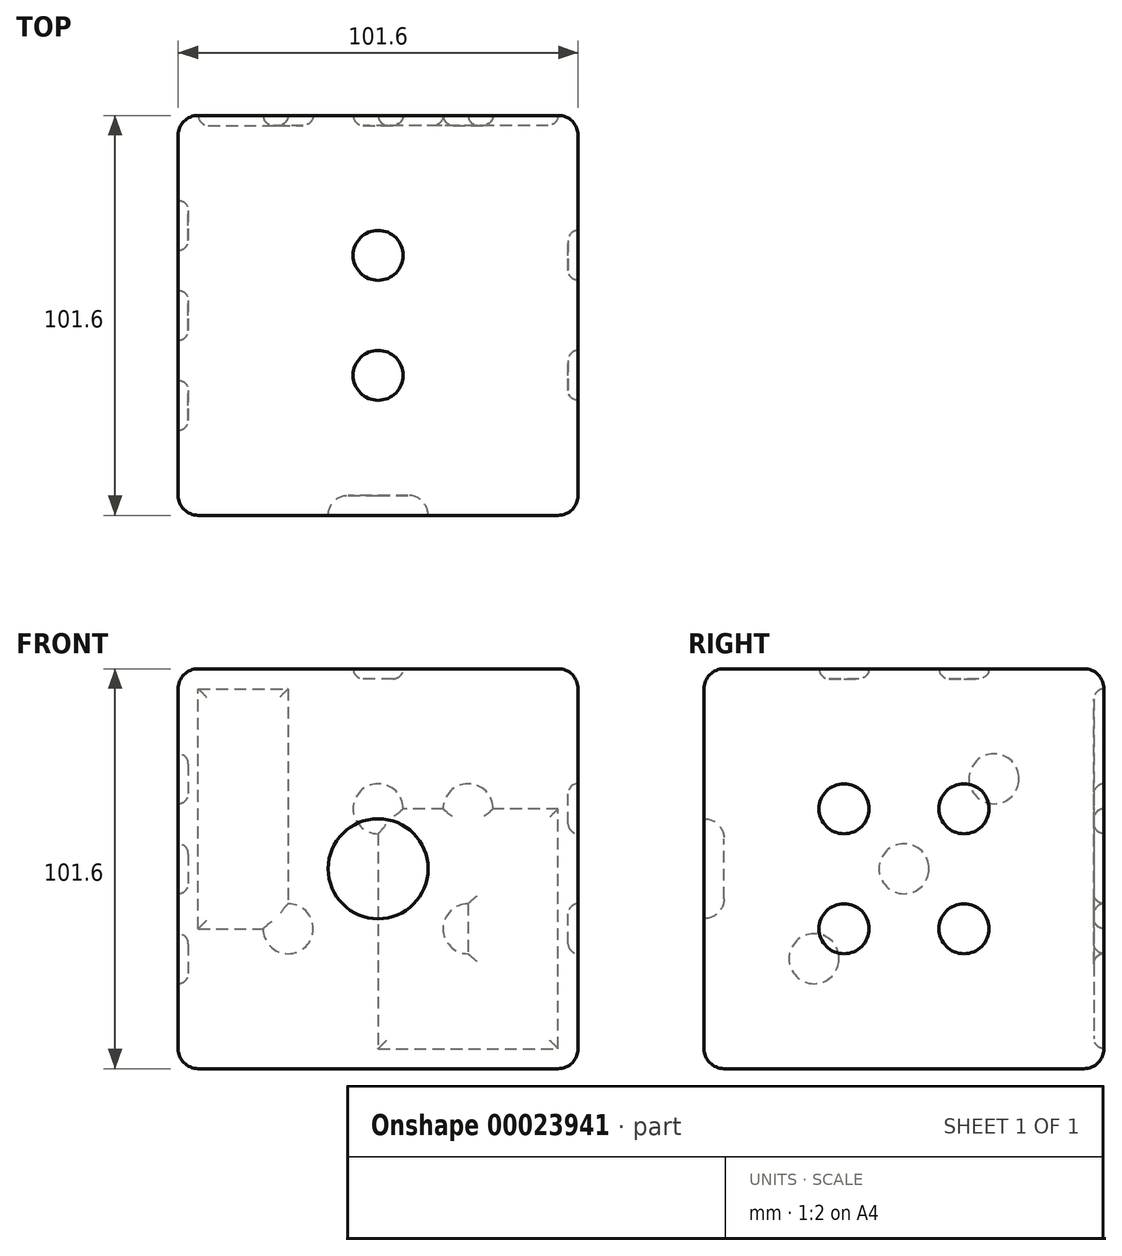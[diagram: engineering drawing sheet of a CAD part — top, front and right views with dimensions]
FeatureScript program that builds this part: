
annotation { "Feature Type Name" : "Feature", "Feature Type Description" : "" }
export const myFeature = defineFeature(function(context is Context, id is Id, definition is map)
    precondition{}
    {
        {
            var Q0;
            Q0=qCreatedBy(makeId("Front.planeOp"),FACE);
            var sketch = newSketch(context, id + "F0", { "sketchPlane" : qUnion([Q0])});
            skLineSegment(sketch, "E0.bottom", {"start": v(0, 0) * mm, "end": v(101.6, 0) * mm});
            skLineSegment(sketch, "E0.top", {"start": v(0, 101.6) * mm, "end": v(101.6, 101.6) * mm});
            skLineSegment(sketch, "E0.left", {"start": v(0, 0) * mm, "end": v(0, 101.6) * mm});
            skLineSegment(sketch, "E0.right", {"start": v(101.6, 0) * mm, "end": v(101.6, 101.6) * mm});
            skSolve(sketch);
        }
        {
            var Q0;
            Q0 = qSketchRegion(id + "F0", true);
            extrude(context, id + "F1", {"entities" : qUnion([Q0]), "depth" : 101.6 * mm});
        }
        {
            var Q0;
            Q0=makeQuery(id+"F1.opExtrude","CAP_FACE",FACE,{"disambiguationData":[OSD([sQuery(id+"F0.wireOp",EDGE,"E0.bottom"),sQuery(id+"F0.wireOp",EDGE,"E0.top"),sQuery(id+"F0.wireOp",EDGE,"E0.left"),sQuery(id+"F0.wireOp",EDGE,"E0.right")])],"isStart":true});
            var Q1;
            Q1=makeQuery(id+"F1.opExtrude","CAP_FACE",FACE,{"disambiguationData":[OSD([sQuery(id+"F0.wireOp",EDGE,"E0.bottom"),sQuery(id+"F0.wireOp",EDGE,"E0.top"),sQuery(id+"F0.wireOp",EDGE,"E0.left"),sQuery(id+"F0.wireOp",EDGE,"E0.right")])],"isStart":false});
            var Q2;
            Q2=makeQuery(id+"F1.opExtrude","SWEPT_FACE",FACE,{"disambiguationData":[OSD([sQuery(id+"F0.wireOp",EDGE,"E0.top")])]});
            var Q3;
            Q3=makeQuery(id+"F1.opExtrude","SWEPT_FACE",FACE,{"disambiguationData":[OSD([sQuery(id+"F0.wireOp",EDGE,"E0.bottom")])]});
            fillet(context, id + "F2", {"entities" : qUnion([Q0, Q1, Q2, Q3]), "radius" : 5.08 * mm, "tangentPropagation" : true, "allowEdgeOverflow" : false});
        }
        {
            var Q0;
            Q0=makeQuery(id+"F1.opExtrude","CAP_FACE",FACE,{"disambiguationData":[OSD([sQuery(id+"F0.wireOp",EDGE,"E0.bottom"),sQuery(id+"F0.wireOp",EDGE,"E0.top"),sQuery(id+"F0.wireOp",EDGE,"E0.left"),sQuery(id+"F0.wireOp",EDGE,"E0.right")])],"isStart":false});
            var sketch = newSketch(context, id + "F3", { "sketchPlane" : qUnion([Q0])});
            skCircle(sketch, "E1", {"center": v(50.8, 50.8) * mm, "radius": 12.7 * mm});
            skSolve(sketch);
        }
        {
            var Q0;
            Q0=makeQuery(id+"F3.imprint","IMPRINT",FACE,{"disambiguationData":[TD([[makeQuery(id+"F3.imprint","IMPRINT",EDGE,{"derivedFrom":sQuery(id+"F3.wireOp",EDGE,"E1")}),1.0]])]});
            extrude(context, id + "F4", {"entities" : qUnion([Q0]), "operationType" : NewBodyOperationType.REMOVE, "oppositeDirection" : true, "depth" : 5.08 * mm});
        }
        {
            var Q0;
            Q0=makeQuery(id+"F4.boolean.opBoolean","COPY",FACE,{"derivedFrom":makeQuery(id+"F4.opExtrude","CAP_FACE",FACE,{"disambiguationData":[OSD([sQuery(id+"F3.wireOp",EDGE,"E1")])],"isStart":false})});
            fillet(context, id + "F5", {"entities" : qUnion([Q0]), "radius" : 5.08 * mm, "tangentPropagation" : true, "allowEdgeOverflow" : false});
        }
        {
            var Q0;
            Q0=makeQuery(id+"F1.opExtrude","CAP_FACE",FACE,{"disambiguationData":[OSD([sQuery(id+"F0.wireOp",EDGE,"E0.bottom"),sQuery(id+"F0.wireOp",EDGE,"E0.top"),sQuery(id+"F0.wireOp",EDGE,"E0.left"),sQuery(id+"F0.wireOp",EDGE,"E0.right")])],"isStart":true});
            var sketch = newSketch(context, id + "F6", { "sketchPlane" : qUnion([Q0])});
            skLineSegment(sketch, "E2", {"start": v(-96.52, 66.04) * mm, "end": v(-5.08, 66.04) * mm});
            skLineSegment(sketch, "E3", {"start": v(-5.08, 35.56) * mm, "end": v(-96.52, 35.56) * mm});
            skLineSegment(sketch, "E4", {"start": v(-73.66, 96.52) * mm, "end": v(-73.66, 5.08) * mm});
            skLineSegment(sketch, "E5", {"start": v(-50.8, 96.52) * mm, "end": v(-50.8, 5.08) * mm});
            skLineSegment(sketch, "E6", {"start": v(-27.94, 96.52) * mm, "end": v(-27.94, 5.08) * mm});
            skCircle(sketch, "E7", {"center": v(-73.66, 66.04) * mm, "radius": 6.35 * mm});
            skCircle(sketch, "E8", {"center": v(-50.8, 66.04) * mm, "radius": 6.35 * mm});
            skCircle(sketch, "E9", {"center": v(-27.94, 66.04) * mm, "radius": 6.35 * mm});
            skCircle(sketch, "E10", {"center": v(-27.94, 35.56) * mm, "radius": 6.35 * mm});
            skCircle(sketch, "E11", {"center": v(-50.8, 35.56) * mm, "radius": 6.35 * mm});
            skCircle(sketch, "E12", {"center": v(-73.66, 35.56) * mm, "radius": 6.35 * mm});
            skSolve(sketch);
        }
        {
            var Q0;
            {var subQ1=sQuery(id+"F6.wireOp",EDGE,"E4");var subQ3=sQuery(id+"F6.wireOp",EDGE,"E2");var subQ5=makeQuery(id+"F6.imprint","INTERSECT",VERTEX,{"derivedFrom":[subQ3,subQ1]});Q0=makeQuery(id+"F6.imprint","IMPRINT",FACE,{"disambiguationData":[TD([[makeQuery(id+"F6.imprint","IMPRINT",EDGE,{"disambiguationData":[TD([[subQ5,-1.0]])],"derivedFrom":subQ3}),1.0]])]});}
            var Q1;
            {var subQ1=sQuery(id+"F6.wireOp",EDGE,"E4");var subQ3=sQuery(id+"F6.wireOp",EDGE,"E2");var subQ5=makeQuery(id+"F6.imprint","INTERSECT",VERTEX,{"derivedFrom":[subQ3,subQ1]});Q1=makeQuery(id+"F6.imprint","IMPRINT",FACE,{"disambiguationData":[TD([[makeQuery(id+"F6.imprint","IMPRINT",EDGE,{"disambiguationData":[TD([[subQ5,-1.0]])],"derivedFrom":subQ3}),-1.0]])]});}
            var Q2;
            {var subQ0=sQuery(id+"F6.wireOp",EDGE,"E7");var subQ3=sQuery(id+"F6.wireOp",EDGE,"E2");var subQ4=makeQuery(id+"F6.imprint","INTERSECT",VERTEX,{"disambiguationData":[OD(0.0)],"derivedFrom":[subQ3,subQ0]});Q2=makeQuery(id+"F6.imprint","IMPRINT",FACE,{"disambiguationData":[TD([[makeQuery(id+"F6.imprint","IMPRINT",EDGE,{"disambiguationData":[TD([[subQ4,-1.0]])],"derivedFrom":subQ3}),-1.0]])]});}
            var Q3;
            {var subQ0=sQuery(id+"F6.wireOp",EDGE,"E7");var subQ3=sQuery(id+"F6.wireOp",EDGE,"E2");var subQ4=makeQuery(id+"F6.imprint","INTERSECT",VERTEX,{"disambiguationData":[OD(0.0)],"derivedFrom":[subQ3,subQ0]});Q3=makeQuery(id+"F6.imprint","IMPRINT",FACE,{"disambiguationData":[TD([[makeQuery(id+"F6.imprint","IMPRINT",EDGE,{"disambiguationData":[TD([[subQ4,-1.0]])],"derivedFrom":subQ3}),1.0]])]});}
            var Q4;
            {var subQ0=sQuery(id+"F6.wireOp",EDGE,"E8");var subQ3=sQuery(id+"F6.wireOp",EDGE,"E2");var subQ4=makeQuery(id+"F6.imprint","INTERSECT",VERTEX,{"disambiguationData":[OD(0.0)],"derivedFrom":[subQ3,subQ0]});Q4=makeQuery(id+"F6.imprint","IMPRINT",FACE,{"disambiguationData":[TD([[makeQuery(id+"F6.imprint","IMPRINT",EDGE,{"disambiguationData":[TD([[subQ4,-1.0]])],"derivedFrom":subQ3}),1.0]])]});}
            var Q5;
            {var subQ1=sQuery(id+"F6.wireOp",EDGE,"E5");var subQ3=sQuery(id+"F6.wireOp",EDGE,"E2");var subQ5=makeQuery(id+"F6.imprint","INTERSECT",VERTEX,{"derivedFrom":[subQ3,subQ1]});Q5=makeQuery(id+"F6.imprint","IMPRINT",FACE,{"disambiguationData":[TD([[makeQuery(id+"F6.imprint","IMPRINT",EDGE,{"disambiguationData":[TD([[subQ5,-1.0]])],"derivedFrom":subQ3}),1.0]])]});}
            var Q6;
            {var subQ1=sQuery(id+"F6.wireOp",EDGE,"E5");var subQ3=sQuery(id+"F6.wireOp",EDGE,"E2");var subQ5=makeQuery(id+"F6.imprint","INTERSECT",VERTEX,{"derivedFrom":[subQ3,subQ1]});Q6=makeQuery(id+"F6.imprint","IMPRINT",FACE,{"disambiguationData":[TD([[makeQuery(id+"F6.imprint","IMPRINT",EDGE,{"disambiguationData":[TD([[subQ5,-1.0]])],"derivedFrom":subQ3}),-1.0]])]});}
            var Q7;
            {var subQ1=sQuery(id+"F6.wireOp",EDGE,"E8");var subQ3=sQuery(id+"F6.wireOp",EDGE,"E2");var subQ5=makeQuery(id+"F6.imprint","INTERSECT",VERTEX,{"disambiguationData":[OD(0.0)],"derivedFrom":[subQ3,subQ1]});Q7=makeQuery(id+"F6.imprint","IMPRINT",FACE,{"disambiguationData":[TD([[makeQuery(id+"F6.imprint","IMPRINT",EDGE,{"disambiguationData":[TD([[subQ5,-1.0]])],"derivedFrom":subQ3}),-1.0]])]});}
            var Q8;
            {var subQ1=sQuery(id+"F6.wireOp",EDGE,"E6");var subQ3=sQuery(id+"F6.wireOp",EDGE,"E2");var subQ5=makeQuery(id+"F6.imprint","INTERSECT",VERTEX,{"derivedFrom":[subQ3,subQ1]});Q8=makeQuery(id+"F6.imprint","IMPRINT",FACE,{"disambiguationData":[TD([[makeQuery(id+"F6.imprint","IMPRINT",EDGE,{"disambiguationData":[TD([[subQ5,-1.0]])],"derivedFrom":subQ3}),1.0]])]});}
            var Q9;
            {var subQ0=sQuery(id+"F6.wireOp",EDGE,"E9");var subQ3=sQuery(id+"F6.wireOp",EDGE,"E2");var subQ4=makeQuery(id+"F6.imprint","INTERSECT",VERTEX,{"disambiguationData":[OD(0.0)],"derivedFrom":[subQ3,subQ0]});Q9=makeQuery(id+"F6.imprint","IMPRINT",FACE,{"disambiguationData":[TD([[makeQuery(id+"F6.imprint","IMPRINT",EDGE,{"disambiguationData":[TD([[subQ4,-1.0]])],"derivedFrom":subQ3}),1.0]])]});}
            var Q10;
            {var subQ0=sQuery(id+"F6.wireOp",EDGE,"E9");var subQ3=sQuery(id+"F6.wireOp",EDGE,"E2");var subQ4=makeQuery(id+"F6.imprint","INTERSECT",VERTEX,{"disambiguationData":[OD(0.0)],"derivedFrom":[subQ3,subQ0]});Q10=makeQuery(id+"F6.imprint","IMPRINT",FACE,{"disambiguationData":[TD([[makeQuery(id+"F6.imprint","IMPRINT",EDGE,{"disambiguationData":[TD([[subQ4,-1.0]])],"derivedFrom":subQ3}),-1.0]])]});}
            var Q11;
            {var subQ1=sQuery(id+"F6.wireOp",EDGE,"E6");var subQ3=sQuery(id+"F6.wireOp",EDGE,"E2");var subQ5=makeQuery(id+"F6.imprint","INTERSECT",VERTEX,{"derivedFrom":[subQ3,subQ1]});Q11=makeQuery(id+"F6.imprint","IMPRINT",FACE,{"disambiguationData":[TD([[makeQuery(id+"F6.imprint","IMPRINT",EDGE,{"disambiguationData":[TD([[subQ5,-1.0]])],"derivedFrom":subQ3}),-1.0]])]});}
            var Q12;
            {var subQ0=sQuery(id+"F6.wireOp",EDGE,"E10");var subQ3=sQuery(id+"F6.wireOp",EDGE,"E3");var subQ4=makeQuery(id+"F6.imprint","INTERSECT",VERTEX,{"disambiguationData":[OD(0.0)],"derivedFrom":[subQ3,subQ0]});Q12=makeQuery(id+"F6.imprint","IMPRINT",FACE,{"disambiguationData":[TD([[makeQuery(id+"F6.imprint","IMPRINT",EDGE,{"disambiguationData":[TD([[subQ4,-1.0]])],"derivedFrom":subQ3}),-1.0]])]});}
            var Q13;
            {var subQ1=sQuery(id+"F6.wireOp",EDGE,"E6");var subQ3=sQuery(id+"F6.wireOp",EDGE,"E3");var subQ5=makeQuery(id+"F6.imprint","INTERSECT",VERTEX,{"derivedFrom":[subQ3,subQ1]});Q13=makeQuery(id+"F6.imprint","IMPRINT",FACE,{"disambiguationData":[TD([[makeQuery(id+"F6.imprint","IMPRINT",EDGE,{"disambiguationData":[TD([[subQ5,-1.0]])],"derivedFrom":subQ3}),-1.0]])]});}
            var Q14;
            {var subQ0=sQuery(id+"F6.wireOp",EDGE,"E6");var subQ3=sQuery(id+"F6.wireOp",EDGE,"E3");var subQ4=makeQuery(id+"F6.imprint","INTERSECT",VERTEX,{"derivedFrom":[subQ3,subQ0]});Q14=makeQuery(id+"F6.imprint","IMPRINT",FACE,{"disambiguationData":[TD([[makeQuery(id+"F6.imprint","IMPRINT",EDGE,{"disambiguationData":[TD([[subQ4,-1.0]])],"derivedFrom":subQ3}),1.0]])]});}
            var Q15;
            {var subQ1=sQuery(id+"F6.wireOp",EDGE,"E10");var subQ3=sQuery(id+"F6.wireOp",EDGE,"E3");var subQ5=makeQuery(id+"F6.imprint","INTERSECT",VERTEX,{"disambiguationData":[OD(0.0)],"derivedFrom":[subQ3,subQ1]});Q15=makeQuery(id+"F6.imprint","IMPRINT",FACE,{"disambiguationData":[TD([[makeQuery(id+"F6.imprint","IMPRINT",EDGE,{"disambiguationData":[TD([[subQ5,-1.0]])],"derivedFrom":subQ3}),1.0]])]});}
            var Q16;
            {var subQ1=sQuery(id+"F6.wireOp",EDGE,"E5");var subQ3=sQuery(id+"F6.wireOp",EDGE,"E3");var subQ5=makeQuery(id+"F6.imprint","INTERSECT",VERTEX,{"derivedFrom":[subQ3,subQ1]});Q16=makeQuery(id+"F6.imprint","IMPRINT",FACE,{"disambiguationData":[TD([[makeQuery(id+"F6.imprint","IMPRINT",EDGE,{"disambiguationData":[TD([[subQ5,-1.0]])],"derivedFrom":subQ3}),-1.0]])]});}
            var Q17;
            {var subQ0=sQuery(id+"F6.wireOp",EDGE,"E11");var subQ3=sQuery(id+"F6.wireOp",EDGE,"E3");var subQ4=makeQuery(id+"F6.imprint","INTERSECT",VERTEX,{"disambiguationData":[OD(0.0)],"derivedFrom":[subQ3,subQ0]});Q17=makeQuery(id+"F6.imprint","IMPRINT",FACE,{"disambiguationData":[TD([[makeQuery(id+"F6.imprint","IMPRINT",EDGE,{"disambiguationData":[TD([[subQ4,-1.0]])],"derivedFrom":subQ3}),-1.0]])]});}
            var Q18;
            {var subQ0=sQuery(id+"F6.wireOp",EDGE,"E11");var subQ3=sQuery(id+"F6.wireOp",EDGE,"E3");var subQ4=makeQuery(id+"F6.imprint","INTERSECT",VERTEX,{"disambiguationData":[OD(0.0)],"derivedFrom":[subQ3,subQ0]});Q18=makeQuery(id+"F6.imprint","IMPRINT",FACE,{"disambiguationData":[TD([[makeQuery(id+"F6.imprint","IMPRINT",EDGE,{"disambiguationData":[TD([[subQ4,-1.0]])],"derivedFrom":subQ3}),1.0]])]});}
            var Q19;
            {var subQ1=sQuery(id+"F6.wireOp",EDGE,"E5");var subQ3=sQuery(id+"F6.wireOp",EDGE,"E3");var subQ5=makeQuery(id+"F6.imprint","INTERSECT",VERTEX,{"derivedFrom":[subQ3,subQ1]});Q19=makeQuery(id+"F6.imprint","IMPRINT",FACE,{"disambiguationData":[TD([[makeQuery(id+"F6.imprint","IMPRINT",EDGE,{"disambiguationData":[TD([[subQ5,-1.0]])],"derivedFrom":subQ3}),1.0]])]});}
            var Q20;
            {var subQ1=sQuery(id+"F6.wireOp",EDGE,"E4");var subQ3=sQuery(id+"F6.wireOp",EDGE,"E3");var subQ5=makeQuery(id+"F6.imprint","INTERSECT",VERTEX,{"derivedFrom":[subQ3,subQ1]});Q20=makeQuery(id+"F6.imprint","IMPRINT",FACE,{"disambiguationData":[TD([[makeQuery(id+"F6.imprint","IMPRINT",EDGE,{"disambiguationData":[TD([[subQ5,-1.0]])],"derivedFrom":subQ3}),-1.0]])]});}
            var Q21;
            {var subQ0=sQuery(id+"F6.wireOp",EDGE,"E12");var subQ3=sQuery(id+"F6.wireOp",EDGE,"E3");var subQ4=makeQuery(id+"F6.imprint","INTERSECT",VERTEX,{"disambiguationData":[OD(0.0)],"derivedFrom":[subQ3,subQ0]});Q21=makeQuery(id+"F6.imprint","IMPRINT",FACE,{"disambiguationData":[TD([[makeQuery(id+"F6.imprint","IMPRINT",EDGE,{"disambiguationData":[TD([[subQ4,-1.0]])],"derivedFrom":subQ3}),-1.0]])]});}
            var Q22;
            {var subQ0=sQuery(id+"F6.wireOp",EDGE,"E12");var subQ3=sQuery(id+"F6.wireOp",EDGE,"E3");var subQ4=makeQuery(id+"F6.imprint","INTERSECT",VERTEX,{"disambiguationData":[OD(0.0)],"derivedFrom":[subQ3,subQ0]});Q22=makeQuery(id+"F6.imprint","IMPRINT",FACE,{"disambiguationData":[TD([[makeQuery(id+"F6.imprint","IMPRINT",EDGE,{"disambiguationData":[TD([[subQ4,-1.0]])],"derivedFrom":subQ3}),1.0]])]});}
            var Q23;
            {var subQ1=sQuery(id+"F6.wireOp",EDGE,"E4");var subQ3=sQuery(id+"F6.wireOp",EDGE,"E3");var subQ5=makeQuery(id+"F6.imprint","INTERSECT",VERTEX,{"derivedFrom":[subQ3,subQ1]});Q23=makeQuery(id+"F6.imprint","IMPRINT",FACE,{"disambiguationData":[TD([[makeQuery(id+"F6.imprint","IMPRINT",EDGE,{"disambiguationData":[TD([[subQ5,-1.0]])],"derivedFrom":subQ3}),1.0]])]});}
            extrude(context, id + "F7", {"entities" : qUnion([Q0, Q1, Q2, Q3, Q4, Q5, Q6, Q7, Q8, Q9, Q10, Q11, Q12, Q13, Q14, Q15, Q16, Q17, Q18, Q19, Q20, Q21, Q22, Q23]), "operationType" : NewBodyOperationType.REMOVE, "oppositeDirection" : true, "depth" : 2.54 * mm});
        }
        {
            var Q0;
            Q0=makeQuery(id+"F7.boolean.opBoolean","COPY",FACE,{"derivedFrom":makeQuery(id+"F7.opExtrude","CAP_FACE",FACE,{"disambiguationData":[OSD([sQuery(id+"F6.wireOp",EDGE,"E9")])],"isStart":false})});
            var Q1;
            Q1=makeQuery(id+"F7.boolean.opBoolean","COPY",FACE,{"derivedFrom":makeQuery(id+"F7.opExtrude","CAP_FACE",FACE,{"disambiguationData":[OSD([sQuery(id+"F6.wireOp",EDGE,"E10")])],"isStart":false})});
            var Q2;
            Q2=makeQuery(id+"F7.boolean.opBoolean","COPY",FACE,{"derivedFrom":makeQuery(id+"F7.opExtrude","CAP_FACE",FACE,{"disambiguationData":[OSD([sQuery(id+"F6.wireOp",EDGE,"E11")])],"isStart":false})});
            var Q3;
            Q3=makeQuery(id+"F7.boolean.opBoolean","COPY",FACE,{"derivedFrom":makeQuery(id+"F7.opExtrude","CAP_FACE",FACE,{"disambiguationData":[OSD([sQuery(id+"F6.wireOp",EDGE,"E12")])],"isStart":false})});
            var Q4;
            Q4=makeQuery(id+"F7.boolean.opBoolean","COPY",FACE,{"derivedFrom":makeQuery(id+"F7.opExtrude","CAP_FACE",FACE,{"disambiguationData":[OSD([sQuery(id+"F6.wireOp",EDGE,"E7")])],"isStart":false})});
            var Q5;
            Q5=makeQuery(id+"F7.boolean.opBoolean","COPY",FACE,{"derivedFrom":makeQuery(id+"F7.opExtrude","CAP_FACE",FACE,{"disambiguationData":[OSD([sQuery(id+"F6.wireOp",EDGE,"E8")])],"isStart":false})});
            fillet(context, id + "F8", {"entities" : qUnion([Q0, Q1, Q2, Q3, Q4, Q5]), "radius" : 2.54 * mm, "tangentPropagation" : true, "allowEdgeOverflow" : false});
        }
        {
            var Q0;
            Q0=makeQuery(id+"F1.opExtrude","SWEPT_FACE",FACE,{"disambiguationData":[OSD([sQuery(id+"F0.wireOp",EDGE,"E0.top")])]});
            var sketch = newSketch(context, id + "F9", { "sketchPlane" : qUnion([Q0])});
            skCircle(sketch, "E13", {"center": v(50.8, -35.56) * mm, "radius": 6.35 * mm});
            skCircle(sketch, "E14", {"center": v(50.8, -66.04) * mm, "radius": 6.35 * mm});
            skPoint(sketch, "E15.orphan", {"position": v(50.8, -5.08) * mm});
            skPoint(sketch, "E16.end.orphan", {"position": v(50.8, -96.52) * mm});
            skSolve(sketch);
        }
        {
            var Q0;
            Q0 = qSketchRegion(id + "F9", true);
            extrude(context, id + "F10", {"entities" : qUnion([Q0]), "operationType" : NewBodyOperationType.REMOVE, "oppositeDirection" : true, "depth" : 2.54 * mm});
        }
        {
            var Q0;
            Q0=makeQuery(id+"F10.boolean.opBoolean","COPY",FACE,{"derivedFrom":makeQuery(id+"F10.opExtrude","CAP_FACE",FACE,{"disambiguationData":[OSD([sQuery(id+"F9.wireOp",EDGE,"E13")])],"isStart":false})});
            var Q1;
            Q1=makeQuery(id+"F10.boolean.opBoolean","COPY",FACE,{"derivedFrom":makeQuery(id+"F10.opExtrude","CAP_FACE",FACE,{"disambiguationData":[OSD([sQuery(id+"F9.wireOp",EDGE,"E14")])],"isStart":false})});
            fillet(context, id + "F11", {"entities" : qUnion([Q0, Q1]), "radius" : 2.54 * mm, "tangentPropagation" : true, "allowEdgeOverflow" : false});
        }
        {
            var Q0;
            Q0=makeQuery(id+"F1.opExtrude","SWEPT_FACE",FACE,{"disambiguationData":[OSD([sQuery(id+"F0.wireOp",EDGE,"E0.right")])]});
            var sketch = newSketch(context, id + "F12", { "sketchPlane" : qUnion([Q0])});
            skCircle(sketch, "E17", {"center": v(-66.04, 66.04) * mm, "radius": 6.35 * mm});
            skCircle(sketch, "E18", {"center": v(-35.56, 66.04) * mm, "radius": 6.35 * mm});
            skCircle(sketch, "E19", {"center": v(-35.56, 35.56) * mm, "radius": 6.35 * mm});
            skCircle(sketch, "E20", {"center": v(-66.04, 35.56) * mm, "radius": 6.35 * mm});
            skSolve(sketch);
        }
        {
            var Q0;
            Q0 = qSketchRegion(id + "F12", true);
            extrude(context, id + "F13", {"entities" : qUnion([Q0]), "operationType" : NewBodyOperationType.REMOVE, "oppositeDirection" : true, "depth" : 2.54 * mm});
        }
        {
            var Q0;
            Q0=makeQuery(id+"F13.boolean.opBoolean","COPY",EDGE,{"derivedFrom":makeQuery(id+"F13.opExtrude","CAP_EDGE",EDGE,{"disambiguationData":[OSD([sQuery(id+"F12.wireOp",EDGE,"E17")])],"isStart":false})});
            var Q1;
            Q1=makeQuery(id+"F13.boolean.opBoolean","COPY",EDGE,{"derivedFrom":makeQuery(id+"F13.opExtrude","CAP_EDGE",EDGE,{"disambiguationData":[OSD([sQuery(id+"F12.wireOp",EDGE,"E18")])],"isStart":false})});
            var Q2;
            Q2=makeQuery(id+"F13.boolean.opBoolean","COPY",FACE,{"derivedFrom":makeQuery(id+"F13.opExtrude","CAP_FACE",FACE,{"disambiguationData":[OSD([sQuery(id+"F12.wireOp",EDGE,"E19")])],"isStart":false})});
            var Q3;
            Q3=makeQuery(id+"F13.boolean.opBoolean","COPY",FACE,{"derivedFrom":makeQuery(id+"F13.opExtrude","CAP_FACE",FACE,{"disambiguationData":[OSD([sQuery(id+"F12.wireOp",EDGE,"E20")])],"isStart":false})});
            fillet(context, id + "F14", {"entities" : qUnion([Q0, Q1, Q2, Q3]), "radius" : 2.54 * mm, "tangentPropagation" : true, "allowEdgeOverflow" : false});
        }
        {
            var Q0;
            Q0=makeQuery(id+"F1.opExtrude","SWEPT_FACE",FACE,{"disambiguationData":[OSD([sQuery(id+"F0.wireOp",EDGE,"E0.left")])]});
            var sketch = newSketch(context, id + "F15", { "sketchPlane" : qUnion([Q0])});
            skCircle(sketch, "E21", {"center": v(27.94, 73.66) * mm, "radius": 6.35 * mm});
            skCircle(sketch, "E22", {"center": v(50.8, 50.8) * mm, "radius": 6.35 * mm});
            skCircle(sketch, "E23", {"center": v(73.66, 27.94) * mm, "radius": 6.35 * mm});
            skSolve(sketch);
        }
        {
            var Q0;
            Q0 = qSketchRegion(id + "F15", true);
            extrude(context, id + "F16", {"entities" : qUnion([Q0]), "operationType" : NewBodyOperationType.REMOVE, "oppositeDirection" : true, "depth" : 2.54 * mm});
        }
        {
            var Q0;
            Q0=makeQuery(id+"F16.boolean.opBoolean","COPY",FACE,{"derivedFrom":makeQuery(id+"F16.opExtrude","CAP_FACE",FACE,{"disambiguationData":[OSD([sQuery(id+"F15.wireOp",EDGE,"E21")])],"isStart":false})});
            var Q1;
            Q1=makeQuery(id+"F16.boolean.opBoolean","COPY",FACE,{"derivedFrom":makeQuery(id+"F16.opExtrude","CAP_FACE",FACE,{"disambiguationData":[OSD([sQuery(id+"F15.wireOp",EDGE,"E22")])],"isStart":false})});
            var Q2;
            Q2=makeQuery(id+"F16.boolean.opBoolean","COPY",FACE,{"derivedFrom":makeQuery(id+"F16.opExtrude","CAP_FACE",FACE,{"disambiguationData":[OSD([sQuery(id+"F15.wireOp",EDGE,"E23")])],"isStart":false})});
            fillet(context, id + "F17", {"entities" : qUnion([Q0, Q1, Q2]), "radius" : 2.54 * mm, "tangentPropagation" : true, "allowEdgeOverflow" : false});
        }
    });
